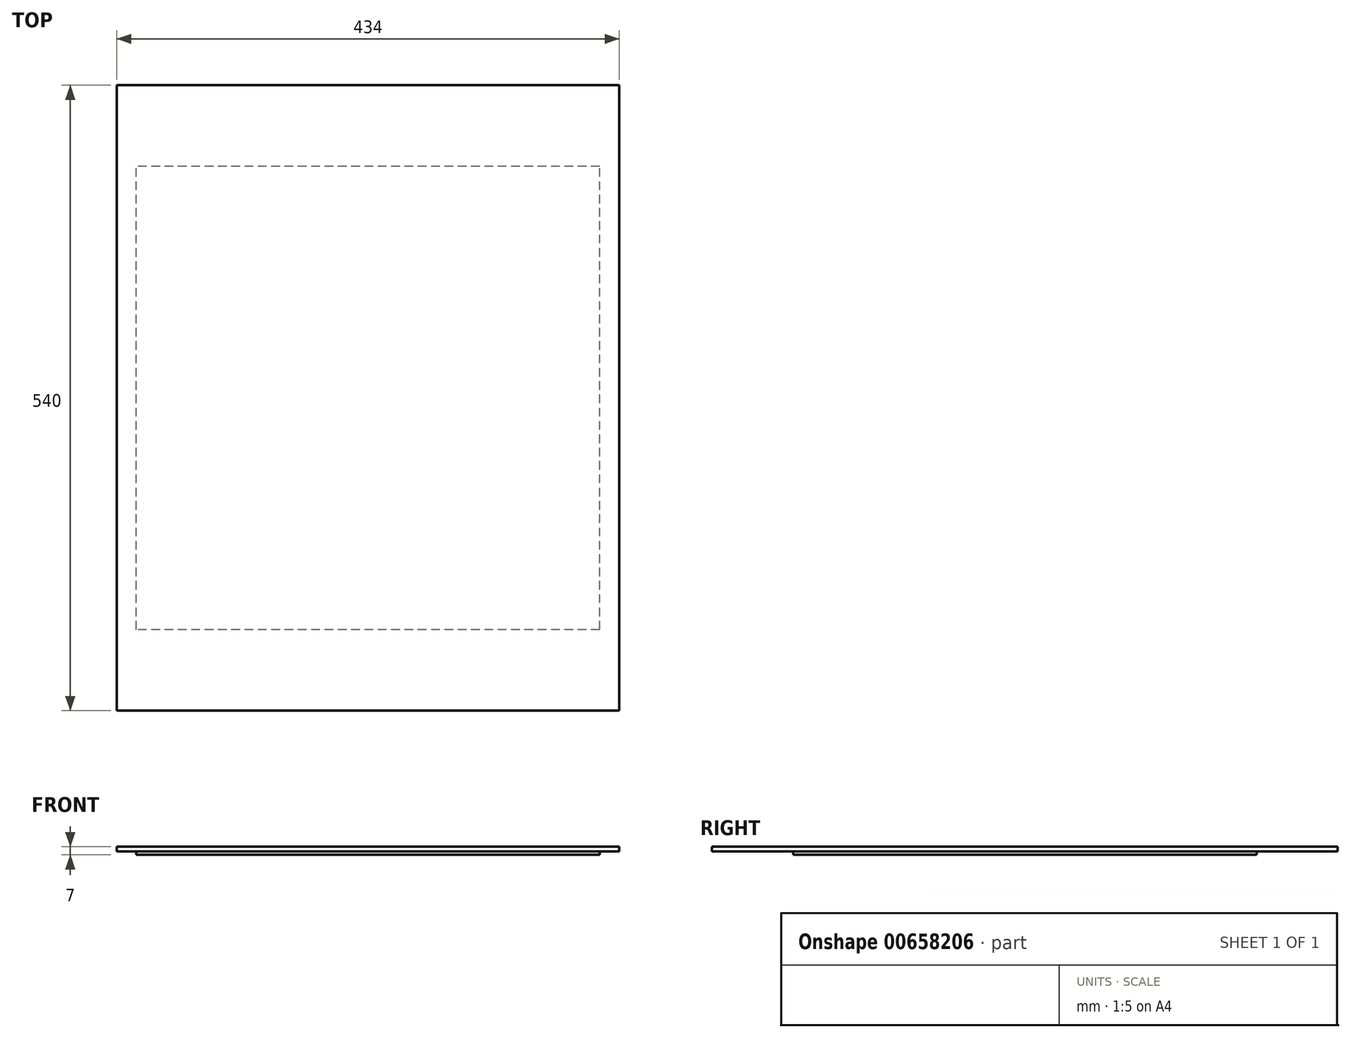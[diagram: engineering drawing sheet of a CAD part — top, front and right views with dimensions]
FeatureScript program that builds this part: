
annotation { "Feature Type Name" : "Feature", "Feature Type Description" : "" }
export const myFeature = defineFeature(function(context is Context, id is Id, definition is map)
    precondition{}
    {
        {
            var Q0;
            Q0=qCreatedBy(makeId("Top.planeOp"),FACE);
            var sketch = newSketch(context, id + "F0", { "sketchPlane" : qUnion([Q0])});
            skLineSegment(sketch, "E0.bottom", {"start": v(200, -200) * mm, "end": v(-200, -200) * mm});
            skLineSegment(sketch, "E0.top", {"start": v(200, 200) * mm, "end": v(-200, 200) * mm});
            skLineSegment(sketch, "E0.left", {"start": v(200, -200) * mm, "end": v(200, 200) * mm});
            skLineSegment(sketch, "E0.right", {"start": v(-200, -200) * mm, "end": v(-200, 200) * mm});
            skPoint(sketch, "E0.middle", {"position": v(0, 0) * mm});
            skSolve(sketch);
        }
        {
            var Q0;
            Q0=makeQuery(id+"F0.imprint","IMPRINT",FACE,{"disambiguationData":[TD([[makeQuery(id+"F0.imprint","IMPRINT",EDGE,{"derivedFrom":sQuery(id+"F0.wireOp",EDGE,"E0.bottom")}),-1.0]])]});
            extrude(context, id + "F1", {"entities" : qUnion([Q0]), "depth" : 3 * mm, "offsetDistance" : 25.4 * mm});
        }
        {
            var Q0;
            Q0=makeQuery(id+"F1.opExtrude","CAP_FACE",FACE,{"disambiguationData":[OSD([sQuery(id+"F0.wireOp",EDGE,"E0.bottom"),sQuery(id+"F0.wireOp",EDGE,"E0.top"),sQuery(id+"F0.wireOp",EDGE,"E0.left"),sQuery(id+"F0.wireOp",EDGE,"E0.right")])],"isStart":false});
            var sketch = newSketch(context, id + "F2", { "sketchPlane" : qUnion([Q0])});
            skLineSegment(sketch, "E1.bottom", {"start": v(217, -270) * mm, "end": v(-217, -270) * mm});
            skLineSegment(sketch, "E1.top", {"start": v(217, 270) * mm, "end": v(-217, 270) * mm});
            skLineSegment(sketch, "E1.left", {"start": v(217, -270) * mm, "end": v(217, 270) * mm});
            skLineSegment(sketch, "E1.right", {"start": v(-217, -270) * mm, "end": v(-217, 270) * mm});
            skPoint(sketch, "E1.middle", {"position": v(0, 0) * mm});
            skSolve(sketch);
        }
        {
            var Q0;
            Q0=makeQuery(id+"F2.imprint","IMPRINT",FACE,{"disambiguationData":[TD([[makeQuery(id+"F2.imprint","IMPRINT",EDGE,{"derivedFrom":sQuery(id+"F2.wireOp",EDGE,"E1.bottom")}),-1.0]])]});
            var Q1;
            Q1=makeQuery(id+"F2.imprint","IMPRINT",FACE,{"disambiguationData":[TD([[makeQuery(id+"F2.imprint","IMPRINT",EDGE,{"derivedFrom":makeQuery(id+"F1.opExtrude","CAP_EDGE",EDGE,{"disambiguationData":[OSD([sQuery(id+"F0.wireOp",EDGE,"E0.bottom")])],"isStart":false})}),-1.0]])]});
            extrude(context, id + "F3", {"entities" : qUnion([Q0, Q1]), "depth" : 4 * mm, "offsetDistance" : 25.4 * mm});
        }
    });
